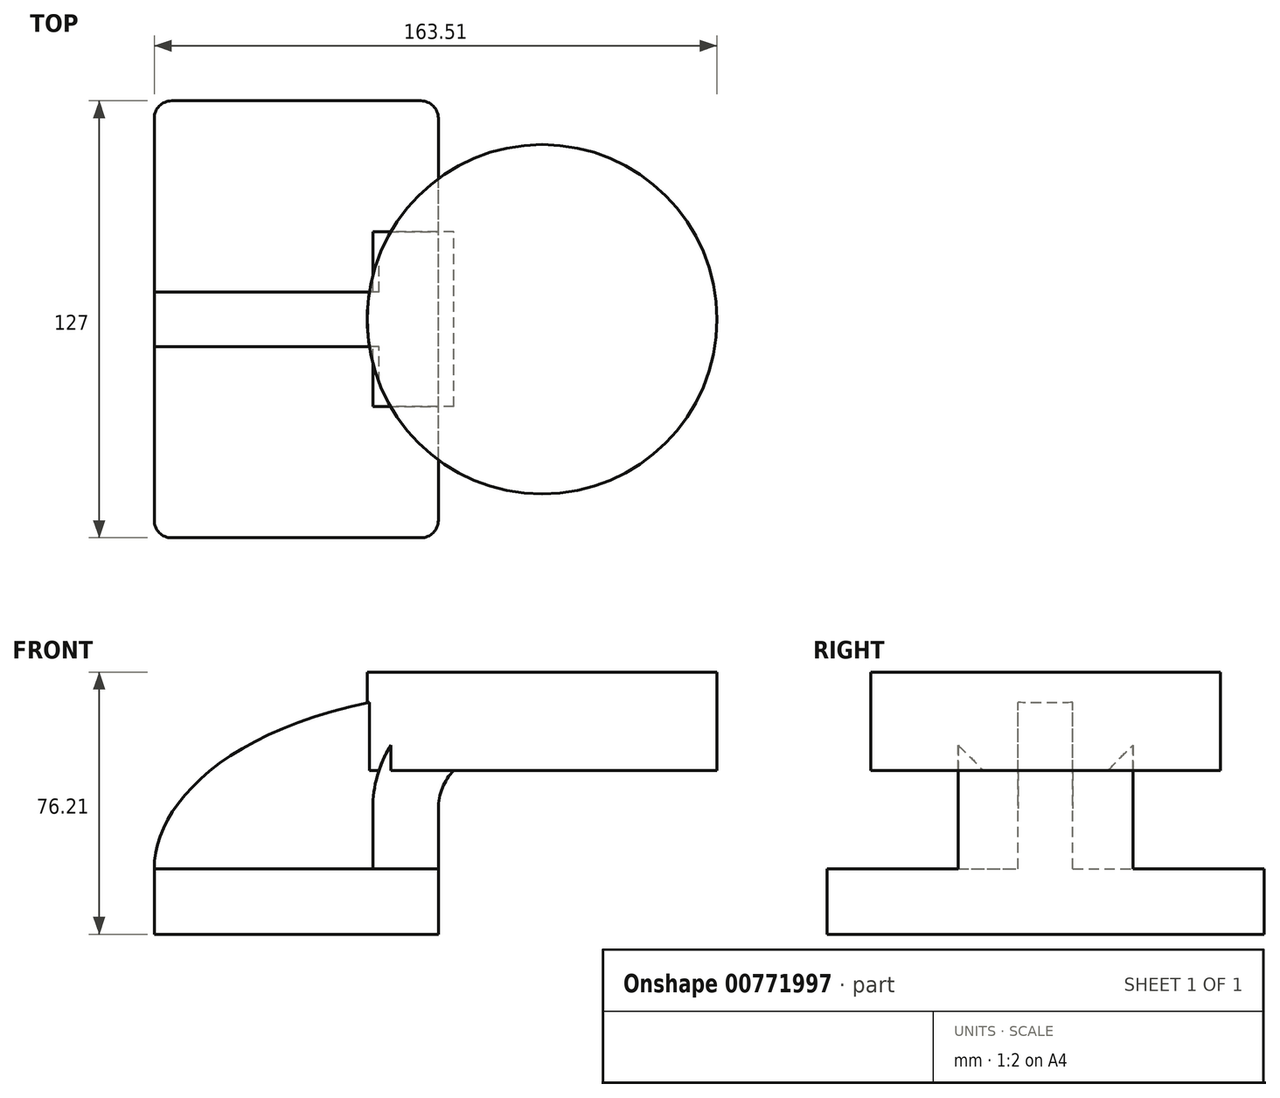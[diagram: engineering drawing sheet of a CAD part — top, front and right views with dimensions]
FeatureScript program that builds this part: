
annotation { "Feature Type Name" : "Feature", "Feature Type Description" : "" }
export const myFeature = defineFeature(function(context is Context, id is Id, definition is map)
    precondition{}
    {
        {
            var Q0;
            Q0=qCreatedBy(makeId("Front.planeOp"),FACE);
            var sketch = newSketch(context, id + "F0", { "sketchPlane" : qUnion([Q0])});
            skLineSegment(sketch, "E0.bottom", {"start": v(-41.28, 9.52) * mm, "end": v(41.27, 9.53) * mm});
            skLineSegment(sketch, "E0.top", {"start": v(-41.28, -9.53) * mm, "end": v(41.28, -9.53) * mm});
            skLineSegment(sketch, "E0.left", {"start": v(-41.28, 9.52) * mm, "end": v(-41.27, -9.53) * mm});
            skLineSegment(sketch, "E0.right", {"start": v(41.28, 9.53) * mm, "end": v(41.28, -9.52) * mm});
            skPoint(sketch, "E0.middle", {"position": v(0, 0) * mm});
            skLineSegment(sketch, "E1.bottom", {"start": v(71.43, 66.67) * mm, "end": v(122.23, 66.67) * mm});
            skLineSegment(sketch, "E1.top", {"start": v(71.43, 38.1) * mm, "end": v(122.23, 38.1) * mm});
            skLineSegment(sketch, "E1.left", {"start": v(71.43, 66.67) * mm, "end": v(71.43, 38.1) * mm});
            skLineSegment(sketch, "E1.right", {"start": v(122.23, 66.67) * mm, "end": v(122.23, 38.1) * mm});
            skLineSegment(sketch, "E2", {"start": v(41.27, 9.53) * mm, "end": v(41.27, 27) * mm});
            skArc(sketch, "E3", {"start": v(41.27, 27) * mm, "mid": v(45.92, 38.23) * mm, "end": v(57.15, 42.88) * mm});
            skLineSegment(sketch, "E4", {"start": v(57.15, 42.88) * mm, "end": v(85.72, 42.88) * mm});
            skLineSegment(sketch, "E5.0", {"start": v(57.15, 61.93) * mm, "end": v(85.72, 61.93) * mm});
            skArc(sketch, "E5.1", {"start": v(22.23, 27) * mm, "mid": v(32.45, 51.7) * mm, "end": v(57.15, 61.93) * mm});
            skLineSegment(sketch, "E5.2", {"start": v(22.22, 9.53) * mm, "end": v(22.22, 27) * mm});
            skLineSegment(sketch, "E6", {"start": v(85.72, 38.1) * mm, "end": v(85.72, 66.67) * mm});
            skFitSpline(sketch, "E7", {"points": [v(-41.28, 9.52) * mm, v(67.88, 61.93) * mm], "startDerivative": vector(-0.24, 67.21) * mm, "endDerivative": vector(233.35, -1.64) * mm});
            skSolve(sketch);
        }
        {
            var Q0;
            Q0=makeQuery(id+"F0.imprint","IMPRINT",FACE,{"disambiguationData":[TD([[makeQuery(id+"F0.imprint","IMPRINT",EDGE,{"derivedFrom":sQuery(id+"F0.wireOp",EDGE,"E0.top")}),1.0]])]});
            extrude(context, id + "F1", {"entities" : qUnion([Q0]), "endBound" : BoundingType.SYMMETRIC, "depth" : 127 * mm, "offsetDistance" : 25.4 * mm});
        }
        {
            var Q0;
            {var subQ1=sQuery(id+"F0.wireOp",EDGE,"E2");Q0=makeQuery(id+"F0.imprint","IMPRINT",FACE,{"disambiguationData":[TD([[makeQuery(id+"F0.imprint","IMPRINT",EDGE,{"derivedFrom":subQ1}),1.0]])]});}
            extrude(context, id + "F2", {"entities" : qUnion([Q0]), "operationType" : NewBodyOperationType.ADD, "endBound" : BoundingType.SYMMETRIC, "depth" : 50.8 * mm, "offsetDistance" : 25.4 * mm});
        }
        {
            var Q0;
            {var subQ3=sQuery(id+"F0.wireOp",EDGE,"E5.2");Q0=makeQuery(id+"F0.imprint","IMPRINT",FACE,{"disambiguationData":[TD([[makeQuery(id+"F0.imprint","IMPRINT",EDGE,{"derivedFrom":subQ3}),1.0]])]});}
            extrude(context, id + "F3", {"entities" : qUnion([Q0]), "operationType" : NewBodyOperationType.ADD, "endBound" : BoundingType.SYMMETRIC, "depth" : 15.88 * mm, "offsetDistance" : 25.4 * mm});
        }
        {
            var Q0;
            {var subQ0=sQuery(id+"F0.wireOp",EDGE,"E1.left");var subQ1=sQuery(id+"F0.wireOp",EDGE,"E1.top");var subQ2=makeQuery(id+"F0.imprint","INTERSECT",VERTEX,{"derivedFrom":[subQ1,subQ0]});Q0=makeQuery(id+"F0.imprint","IMPRINT",FACE,{"disambiguationData":[TD([[makeQuery(id+"F0.imprint","IMPRINT",EDGE,{"disambiguationData":[TD([[subQ2,-1.0]])],"derivedFrom":subQ1}),1.0]])]});}
            var Q1;
            {var subQ0=sQuery(id+"F0.wireOp",EDGE,"E1.left");var subQ1=sQuery(id+"F0.wireOp",EDGE,"E1.bottom");var subQ2=makeQuery(id+"F0.imprint","INTERSECT",VERTEX,{"derivedFrom":[subQ1,subQ0]});Q1=makeQuery(id+"F0.imprint","IMPRINT",FACE,{"disambiguationData":[TD([[makeQuery(id+"F0.imprint","IMPRINT",EDGE,{"disambiguationData":[TD([[subQ2,-1.0]])],"derivedFrom":subQ1}),-1.0]])]});}
            var Q2;
            {var subQ0=sQuery(id+"F0.wireOp",EDGE,"E5.0");var subQ1=sQuery(id+"F0.wireOp",EDGE,"E1.left");var subQ2=makeQuery(id+"F0.imprint","INTERSECT",VERTEX,{"derivedFrom":[subQ1,subQ0]});Q2=makeQuery(id+"F0.imprint","IMPRINT",FACE,{"disambiguationData":[TD([[makeQuery(id+"F0.imprint","IMPRINT",EDGE,{"disambiguationData":[TD([[subQ2,-1.0]])],"derivedFrom":subQ1}),1.0]])]});}
            var Q3;
            {var subQ4=sQuery(id+"F0.wireOp",EDGE,"E1.right");Q3=makeQuery(id+"F0.imprint","IMPRINT",FACE,{"disambiguationData":[TD([[makeQuery(id+"F0.imprint","IMPRINT",EDGE,{"derivedFrom":subQ4}),-1.0]])]});}
            var Q4;
            Q4=sQuery(id+"F0.wireOp",EDGE,"E1.left");
            revolve(context, id + "F4", {"operationType" : NewBodyOperationType.ADD, "surfaceOperationType" : NewSurfaceOperationType.NEW, "entities" : qUnion([Q0, Q1, Q2, Q3]), "axis" : qUnion([Q4]), "revolveType" : RevolveType.FULL});
        }
        {
            var Q0;
            Q0=makeQuery(id+"F1.opExtrude","CAP_EDGE",EDGE,{"disambiguationData":[OSD([sQuery(id+"F0.wireOp",EDGE,"E0.right")])],"isStart":false});
            var Q1;
            Q1=makeQuery(id+"F1.opExtrude","CAP_EDGE",EDGE,{"disambiguationData":[OSD([sQuery(id+"F0.wireOp",EDGE,"E0.left")])],"isStart":false});
            var Q2;
            Q2=makeQuery(id+"F1.opExtrude","CAP_EDGE",EDGE,{"disambiguationData":[OSD([sQuery(id+"F0.wireOp",EDGE,"E0.right")])],"isStart":true});
            var Q3;
            Q3=makeQuery(id+"F1.opExtrude","CAP_EDGE",EDGE,{"disambiguationData":[OSD([sQuery(id+"F0.wireOp",EDGE,"E0.left")])],"isStart":true});
            fillet(context, id + "F5", {"entities" : qUnion([Q0, Q1, Q2, Q3]), "radius" : 5.08 * mm, "tangentPropagation" : true, "allowEdgeOverflow" : false});
        }
    });
